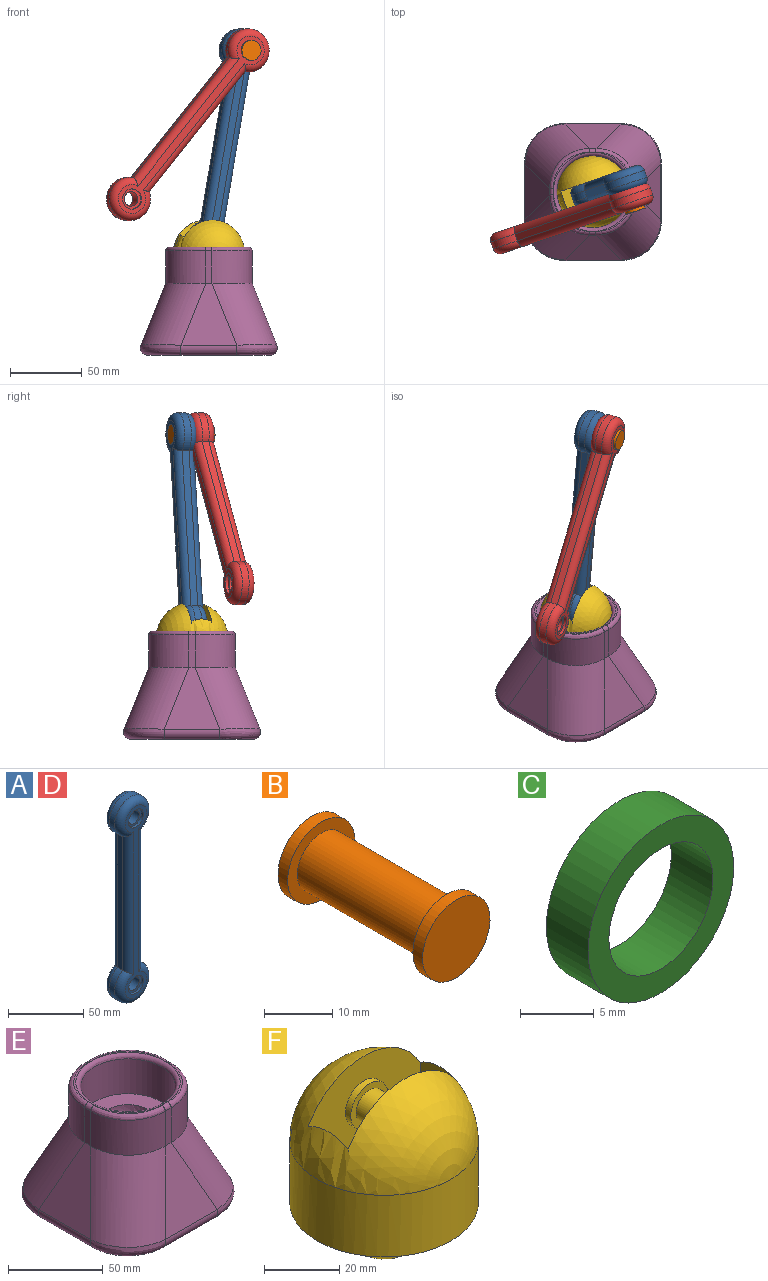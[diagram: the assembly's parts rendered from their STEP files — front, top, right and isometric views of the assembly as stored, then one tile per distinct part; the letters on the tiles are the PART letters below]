
ASSEMBLY  parts=6 mates=6
PART A: 24 faces, bbox 32.5x15x167.5 mm
  f0: cylinder r=5mm len=11mm, axis (0,-1,0), area 345.6mm2, adj f19,f22
  f1: cylinder r=5mm len=11mm, axis (0,-1,0), area 345.6mm2, adj f17,f20
  f2: plane 109.02x5mm, normal (1,0,0), area 545.1mm2, adj f3,f5,f8,f12
  f3: cylinder r=15mm len=30mm, axis (0,1,0), area 392.7mm2, adj f2,f4,f9,f13
  f4: plane 109.02x5mm, normal (-1,0,0), area 545.1mm2, adj f3,f5,f11,f15
  f5: cylinder r=15mm len=30mm, axis (0,1,0), area 392.7mm2, adj f2,f4,f10,f14
  f6: plane 155x20mm, normal (0,-1,0), area 896.5mm2, adj f12,f13,f14,f15,f16,f18
  f7: plane 155x20mm, normal (0,1,0), area 896.5mm2, adj f8,f9,f10,f11,f21,f23
  f8: cylinder r=5mm len=115.64mm, axis (0,0,1), area 874.1mm2, adj f2,f7,f9,f10
  f9: torus R=10mm, axis (0,-1,0), area 558mm2, adj f3,f7,f8,f11
  f10: torus R=10mm, axis (0,-1,0), area 558mm2, adj f5,f7,f8,f11
  f11: cylinder r=5mm len=115.64mm, axis (0,0,-1), area 874.1mm2, adj f4,f7,f9,f10
  f12: cylinder r=5mm len=115.64mm, axis (0,0,-1), area 874.1mm2, adj f2,f6,f13,f14
  f13: torus R=10mm, axis (0,-1,0), area 558mm2, adj f3,f6,f12,f15
  f14: torus R=10mm, axis (0,-1,0), area 558mm2, adj f5,f6,f12,f15
  f15: cylinder r=5mm len=115.64mm, axis (0,0,1), area 874.1mm2, adj f4,f6,f13,f14
  f16: cylinder r=7mm len=14mm, axis (0,-1,0), area 88mm2, adj f6,f17
  f17: plane 14x14mm, normal (0,-1,0), area 75.4mm2, adj f1,f16
  f18: cylinder r=7mm len=14mm, axis (0,-1,0), area 88mm2, adj f6,f19
  f19: plane 14x14mm, normal (0,-1,0), area 75.4mm2, adj f0,f18
  f20: plane 14x14mm, normal (0,1,0), area 75.4mm2, adj f1,f21
  f21: cylinder r=7mm len=14mm, axis (0,1,0), area 88mm2, adj f7,f20
  f22: plane 14x14mm, normal (0,1,0), area 75.4mm2, adj f0,f23
  f23: cylinder r=7mm len=14mm, axis (0,1,0), area 88mm2, adj f7,f22
PART B: 7 faces, bbox 14x30x14 mm
  f0: plane 14x14mm, normal (0,1,0), area 75.4mm2, adj f1,f6
  f1: cylinder r=5mm len=26mm, axis (0,1,0), area 816.8mm2, adj f0,f2
  f2: plane 14x14mm, normal (0,-1,0), area 75.4mm2, adj f1,f3
  f3: cylinder r=7mm len=14mm, axis (0,1,0), area 88mm2, adj f2,f4
  f4: plane 14x14mm, normal (0,1,0), area 153.9mm2, adj f3
  f5: plane 14x14mm, normal (0,-1,0), area 153.9mm2, adj f6
  f6: cylinder r=7mm len=14mm, axis (0,1,0), area 88mm2, adj f0,f5
PART C: 4 faces, bbox 14x4x14 mm
  f0: cylinder r=5mm len=10mm, axis (0,-1,0), area 125.7mm2, adj f2,f3
  f1: cylinder r=7mm len=14mm, axis (0,-1,0), area 175.9mm2, adj f2,f3
  f2: plane 14x14mm, normal (0,1,0), area 75.4mm2, adj f0,f1
  f3: plane 14x14mm, normal (0,-1,0), area 75.4mm2, adj f0,f1
PART D: same geometry as A
PART E: 41 faces, bbox 100.2x100.2x75 mm
  f0: plane 27.5x27.5mm, normal (0,0,1), area 30.8mm2, adj f32,f33,f34,f35
  f1: plane 27.5x27.5mm, normal (0,0,1), area 30.8mm2, adj f32,f34,f36,f38
  f2: plane 27.5x27.5mm, normal (0,0,1), area 30.8mm2, adj f32,f38,f39,f40
  f3: plane 85.23x85.23mm, normal (0,0,-1), area 6821.3mm2, adj f8,f9,f10,f11,f13,f15,f17,f19
  f4: plane 43.14x38.81mm, normal (0,-0.93,0.37), area 1001.3mm2, adj f10,f14,f18,f21
  f5: plane 43.14x38.81mm, normal (0.93,0,0.37), area 1001.3mm2, adj f8,f16,f18,f23
  f6: plane 43.14x38.81mm, normal (0,0.93,0.37), area 1001.3mm2, adj f9,f12,f16,f25
  f7: plane 43.14x38.81mm, normal (-0.93,0,0.37), area 1001.3mm2, adj f11,f12,f14,f28
  f8: cylinder r=5mm len=38.81mm, axis (0,-1,0), area 378.6mm2, adj f3,f5,f17,f19
  f9: cylinder r=5mm len=38.81mm, axis (-1,0,0), area 378.6mm2, adj f3,f6,f13,f17
  f10: cylinder r=5mm len=38.81mm, axis (-1,0,0), area 378.6mm2, adj f3,f4,f15,f19
  f11: cylinder r=5mm len=38.81mm, axis (0,-1,0), area 378.6mm2, adj f3,f7,f13,f15
  f12: cylinder r=30mm len=49.81mm, axis (0.35,-0.35,0.87), area 2110.3mm2, adj f6,f7,f13,f26
  f13: bspline ~34.54x34.54mm, area 430.9mm2, adj f3,f9,f11,f12
  f14: cylinder r=30mm len=49.81mm, axis (-0.35,-0.35,-0.87), area 2110.3mm2, adj f4,f7,f15,f20
  f15: bspline ~28.22x28.22mm, area 430.9mm2, adj f3,f10,f11,f14
  f16: cylinder r=30mm len=49.81mm, axis (0.35,0.35,-0.87), area 2110.3mm2, adj f5,f6,f17,f24
  f17: bspline ~28.22x28.22mm, area 430.9mm2, adj f3,f8,f9,f16
  f18: cylinder r=30mm len=49.81mm, axis (-0.35,0.35,0.87), area 2110.3mm2, adj f4,f5,f19,f22
  f19: bspline ~34.54x34.54mm, area 430.9mm2, adj f3,f8,f10,f18
  f20: extruded ~27.85x27.85mm, area 990.3mm2, adj f14,f21,f28,f37
  f21: plane 22.5x4.29mm, normal (0,-1,0), area 96.6mm2, adj f4,f20,f22,f35
  f22: extruded ~27.85x27.85mm, area 990.3mm2, adj f18,f21,f23,f33
  f23: plane 22.5x4.29mm, normal (1,0,0), area 96.6mm2, adj f5,f22,f24,f34
  f24: extruded ~27.85x27.85mm, area 990.3mm2, adj f16,f23,f25,f36
  f25: plane 22.5x4.29mm, normal (0,1,0), area 96.6mm2, adj f6,f24,f26,f38
  f26: extruded ~27.85x27.85mm, area 990.3mm2, adj f12,f25,f28,f40
  f27: cylinder r=25mm len=50mm, axis (0,0,-1), area 3534.3mm2, adj f31,f32
  f28: plane 22.5x4.29mm, normal (-1,0,0), area 96.6mm2, adj f7,f20,f26,f39
  f29: plane 27.5x27.5mm, normal (0,0,1), area 30.8mm2, adj f32,f35,f37,f39
  f30: sphere r=15mm, area 1413.7mm2, adj f31
  f31: plane 50x50mm, normal (0,0,1), area 1256.6mm2, adj f27,f30
  f32: torus R=27.5mm, axis (0,0,1), area 639.3mm2, adj f0,f1,f2,f27,f29
  f33: bspline ~32.23x32.23mm, area 167.2mm2, adj f0,f22,f34,f35
  f34: cylinder r=2.5mm len=4.29mm, axis (0,-1,0), area 16.9mm2, adj f0,f1,f23,f33,f36
  f35: cylinder r=2.5mm len=4.29mm, axis (-1,0,0), area 16.9mm2, adj f0,f21,f29,f33,f37
  f36: bspline ~32.23x32.23mm, area 167.2mm2, adj f1,f24,f34,f38
  f37: bspline ~32.23x32.23mm, area 167.2mm2, adj f20,f29,f35,f39
  f38: cylinder r=2.5mm len=4.29mm, axis (1,0,0), area 16.9mm2, adj f1,f2,f25,f36,f40
  f39: cylinder r=2.5mm len=4.29mm, axis (0,1,0), area 16.9mm2, adj f2,f28,f29,f37,f40
  f40: bspline ~32.23x32.23mm, area 167.2mm2, adj f2,f26,f38,f39
PART F: 14 faces, bbox 50x50x60 mm
  f0: sphere r=25mm, area 3160.2mm2, adj f1,f4,f5,f6,f7
  f1: cylinder r=25mm len=50mm, axis (0,0,1), area 3141.6mm2, adj f0,f2
  f2: plane 50x50mm, normal (0,0,-1), area 1256.6mm2, adj f1,f3
  f3: sphere r=15mm, area 1413.7mm2, adj f2
  f4: plane 28.56x15mm, normal (-1,0,0), area 417.6mm2, adj f0,f5,f7,f8
  f5: plane 42x38.85mm, normal (0,1,0), area 1326mm2, adj f0,f4,f6,f8,f9
  f6: plane 28.56x15mm, normal (1,0,0), area 417.6mm2, adj f0,f5,f7,f8
  f7: plane 42x38.85mm, normal (0,-1,0), area 1326mm2, adj f0,f4,f6,f8,f12
  f8: plane 42x15mm, normal (0,0,1), area 630mm2, adj f4,f5,f6,f7
  f9: cylinder r=7mm len=14mm, axis (0,-1,0), area 88mm2, adj f5,f10
  f10: plane 14x14mm, normal (0,1,0), area 75.4mm2, adj f9,f11
  f11: cylinder r=5mm len=11mm, axis (0,-1,0), area 345.6mm2, adj f10,f13
  f12: cylinder r=7mm len=14mm, axis (0,1,0), area 88mm2, adj f7,f13
  f13: plane 14x14mm, normal (0,-1,0), area 75.4mm2, adj f11,f12
PLACE A rot(axis=(0.98,0.16,-0.09),178.4deg) t=(-127.68,-63.17,188.42)mm
PLACE B rot(axis=(-0.08,0.47,0.88),21.2deg) t=(-231.32,-144.21,210.19)mm
PLACE C rot(axis=(-0.08,0.47,0.88),21.2deg) t=(-281.96,-154.86,219.33)mm
PLACE D rot(axis=(-0.15,0.9,0.41),44deg) t=(-181.48,-79.19,151.03)mm
PLACE E t=(-70.33,-69.07,-48.5)mm fixed
PLACE F rot(axis=(0,0,-1),161.4deg) t=(-139.49,-7.28,21.5)mm
MATE planar F.f1 <-> E.f27  axis (0,0,-1) through (-20.33,-19.07,1.5)mm
MATE revolute A.f1 <-> F.f9  axis (0.32,-0.95,0) through (-18.57,-24.28,30.35)mm
MATE revolute C.f0 <-> A.f0  axis (0.32,-0.95,0) through (4.49,-18.62,163.26)mm
MATE ball F.f1 <-> E.f27  axis (0,0,1) through (-20.33,-19.07,1.5)mm
MATE fastened A.f0 <-> A.f0  axis (-0.32,0.95,0) through (0.34,-6.3,163.26)mm
MATE revolute D.f1 <-> B.f1  axis (-0.32,0.95,0) through (4.49,-18.62,163.26)mm
